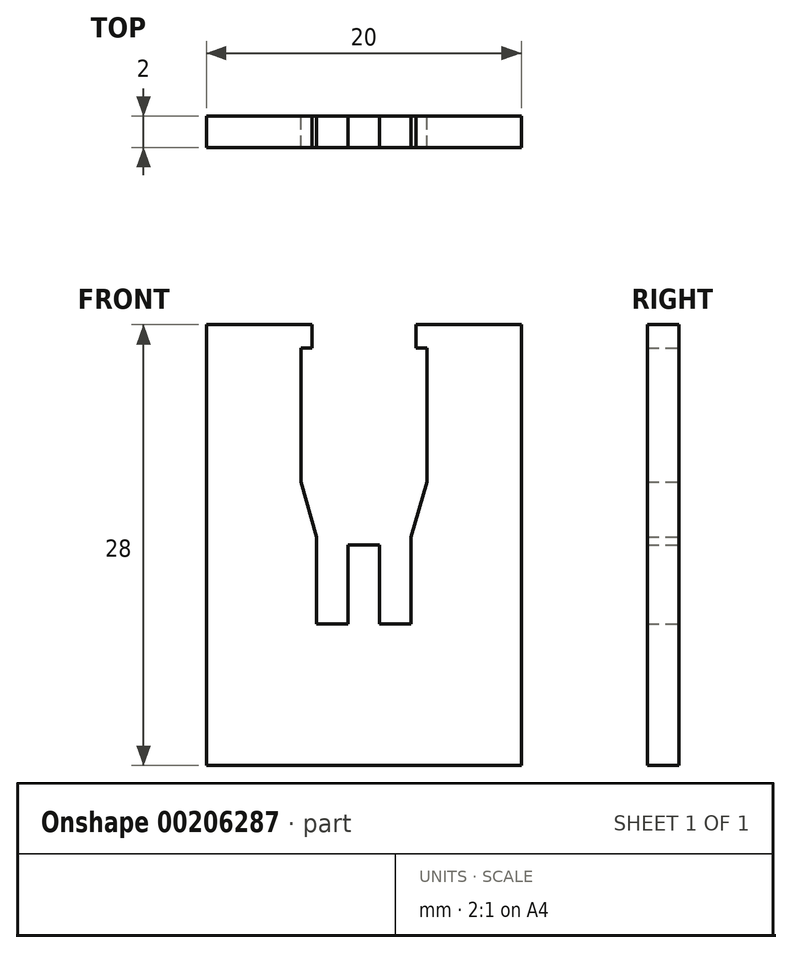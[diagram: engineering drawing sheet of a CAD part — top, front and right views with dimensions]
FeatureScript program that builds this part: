
annotation { "Feature Type Name" : "Feature", "Feature Type Description" : "" }
export const myFeature = defineFeature(function(context is Context, id is Id, definition is map)
    precondition{}
    {
        {
            var Q0;
            Q0=qCreatedBy(makeId("Front.planeOp"),FACE);
            var sketch = newSketch(context, id + "F0", { "sketchPlane" : qUnion([Q0])});
            skLineSegment(sketch, "E0.bottom", {"start": v(10, -14) * mm, "end": v(-10, -14) * mm});
            skLineSegment(sketch, "E0.top", {"start": v(10, 14) * mm, "end": v(-10, 14) * mm});
            skLineSegment(sketch, "E0.left", {"start": v(10, -14) * mm, "end": v(10, 14) * mm});
            skLineSegment(sketch, "E0.right", {"start": v(-10, -14) * mm, "end": v(-10, 14) * mm});
            skPoint(sketch, "E0.middle", {"position": v(0, 0) * mm});
            skLineSegment(sketch, "E1", {"start": v(0, 14) * mm, "end": v(0, -14) * mm, "construction": true});
            skLineSegment(sketch, "E2", {"start": v(-3.3, 14) * mm, "end": v(-3.3, 12.5) * mm});
            skLineSegment(sketch, "E3", {"start": v(-3.3, 12.5) * mm, "end": v(-4, 12.5) * mm});
            skLineSegment(sketch, "E4", {"start": v(-4, 12.5) * mm, "end": v(-4, 4) * mm});
            skLineSegment(sketch, "E5", {"start": v(-3.3, 14) * mm, "end": v(-10, 14) * mm});
            skLineSegment(sketch, "E6", {"start": v(-3, -5) * mm, "end": v(-3, 0.5) * mm});
            skLineSegment(sketch, "E7", {"start": v(-1, -5) * mm, "end": v(-1, 0) * mm});
            skLineSegment(sketch, "E8", {"start": v(-4, 4) * mm, "end": v(-3, 0.5) * mm});
            skLineSegment(sketch, "E9", {"start": v(-3, -5) * mm, "end": v(-1, -5) * mm});
            skLineSegment(sketch, "E10", {"start": v(-1, 0) * mm, "end": v(0, 0) * mm});
            skLineSegment(sketch, "E11.MirrorCS", {"start": v(1, 0) * mm, "end": v(0, 0) * mm});
            skLineSegment(sketch, "E12.MirrorCS", {"start": v(1, -5) * mm, "end": v(1, 0) * mm});
            skLineSegment(sketch, "E13.MirrorCS", {"start": v(3, -5) * mm, "end": v(3, 0.5) * mm});
            skLineSegment(sketch, "E14.MirrorCS", {"start": v(4, 4) * mm, "end": v(3, 0.5) * mm});
            skLineSegment(sketch, "E15.MirrorCS", {"start": v(4, 12.5) * mm, "end": v(4, 4) * mm});
            skLineSegment(sketch, "E16.MirrorCS", {"start": v(3.3, 12.5) * mm, "end": v(4, 12.5) * mm});
            skLineSegment(sketch, "E17.MirrorCS", {"start": v(3.3, 14) * mm, "end": v(3.3, 12.5) * mm});
            skLineSegment(sketch, "E18.MirrorCS", {"start": v(3.3, 14) * mm, "end": v(10, 14) * mm});
            skLineSegment(sketch, "E19.MirrorCS", {"start": v(3, -5) * mm, "end": v(1, -5) * mm});
            skSolve(sketch);
        }
        {
            var Q0;
            Q0=makeQuery(id+"F0.imprint","IMPRINT",FACE,{"disambiguationData":[TD([[makeQuery(id+"F0.imprint","IMPRINT",EDGE,{"derivedFrom":sQuery(id+"F0.wireOp",EDGE,"E0.bottom")}),-1.0]])]});
            extrude(context, id + "F1", {"entities" : qUnion([Q0]), "depth" : 2 * mm});
        }
    });
